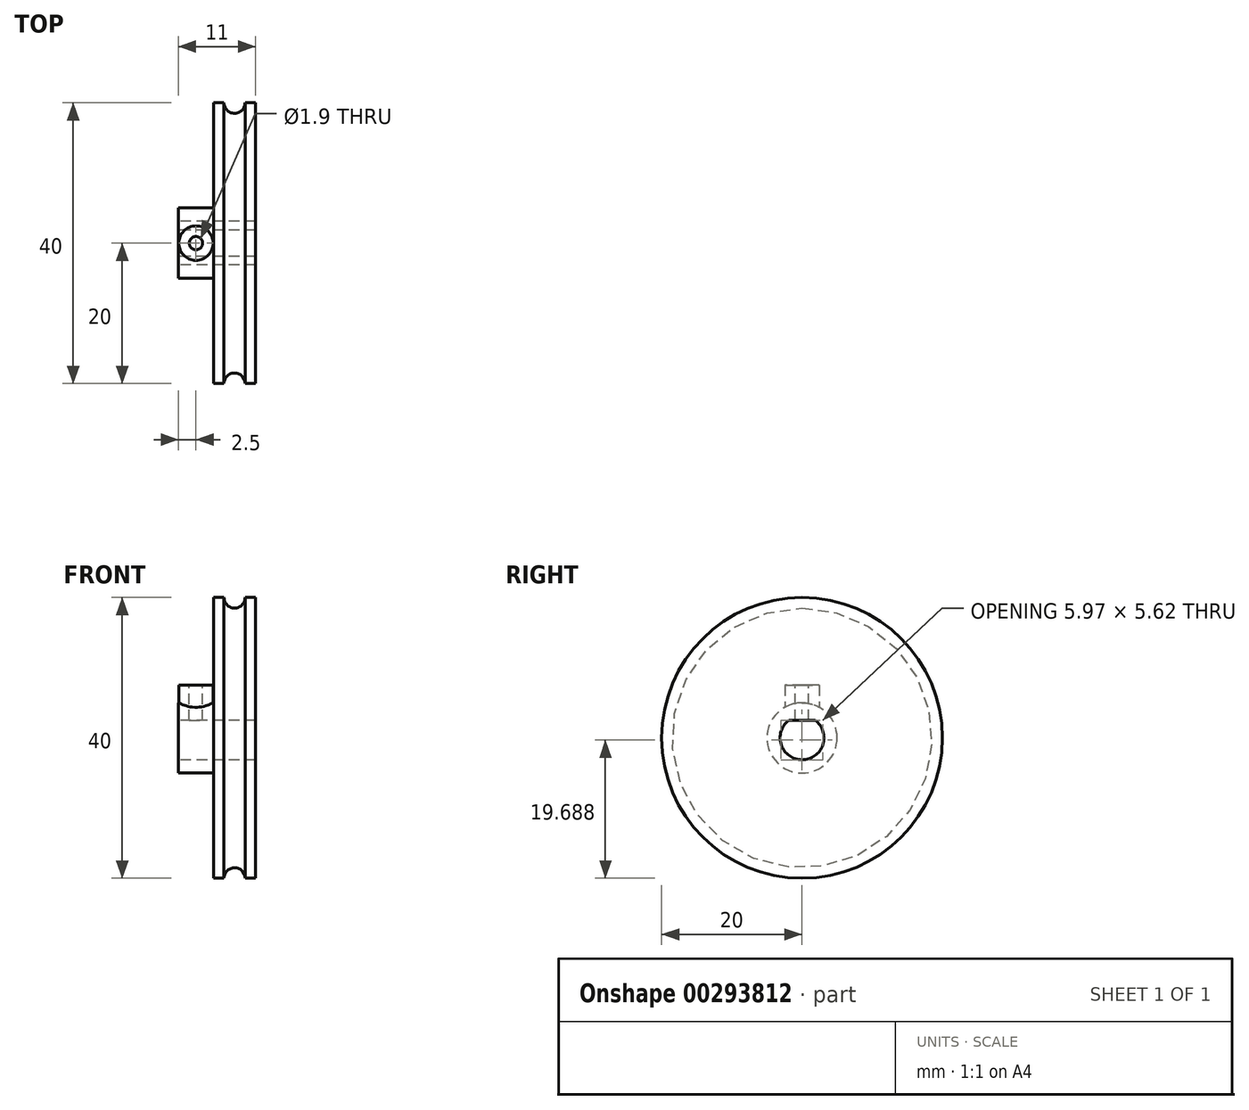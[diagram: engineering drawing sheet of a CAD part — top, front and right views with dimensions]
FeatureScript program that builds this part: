
annotation { "Feature Type Name" : "Feature", "Feature Type Description" : "" }
export const myFeature = defineFeature(function(context is Context, id is Id, definition is map)
    precondition{}
    {
        {
            var Q0;
            Q0=qCreatedBy(makeId("Top.planeOp"),FACE);
            var sketch = newSketch(context, id + "F0", { "sketchPlane" : qUnion([Q0])});
            skLineSegment(sketch, "E0", {"start": v(1.5, 0) * mm, "end": v(1.5, 20) * mm});
            skLineSegment(sketch, "E1", {"start": v(-4.5, 0) * mm, "end": v(-4.5, 20) * mm});
            skLineSegment(sketch, "E2", {"start": v(-4.5, 0) * mm, "end": v(1.5, 0) * mm});
            skLineSegment(sketch, "E3", {"start": v(-4.5, 20) * mm, "end": v(-3, 20) * mm});
            skLineSegment(sketch, "E4", {"start": v(1.5, 20) * mm, "end": v(0, 20) * mm});
            skArc(sketch, "E5", {"start": v(-3, 20) * mm, "mid": v(-1.5, 18.5) * mm, "end": v(0, 20) * mm});
            skSolve(sketch);
        }
        {
            var Q0;
            Q0 = qSketchRegion(id + "F0", true);
            var Q1;
            Q1=sQuery(id+"F0.wireOp",EDGE,"E2");
            revolve(context, id + "F1", {"entities" : qUnion([Q0]), "axis" : qUnion([Q1]), "revolveType" : RevolveType.FULL});
        }
        {
            var Q0;
            Q0=makeQuery(id+"F1.opRevolve","SWEPT_FACE",FACE,{"disambiguationData":[OSD([sQuery(id+"F0.wireOp",EDGE,"E1")])]});
            cPlane(context, id + "F2", {"entities" : qUnion([Q0]), "cplaneType" : CPlaneType.OFFSET, "offset" : 0 * mm, "width" : 150 * mm, "height" : 150 * mm});
        }
        {
            var Q0;
            Q0=qCreatedBy(id+"F2.planeOp",FACE);
            var sketch = newSketch(context, id + "F3", { "sketchPlane" : qUnion([Q0])});
            skCircle(sketch, "E6", {"center": v(0, 0) * mm, "radius": 5 * mm});
            skSolve(sketch);
        }
        {
            var Q0;
            Q0 = qSketchRegion(id + "F3", true);
            extrude(context, id + "F4", {"entities" : qUnion([Q0]), "operationType" : NewBodyOperationType.ADD, "depth" : 5 * mm});
        }
        {
            var Q0;
            Q0=makeQuery(id+"F4.opExtrude","CAP_FACE",FACE,{"disambiguationData":[OSD([sQuery(id+"F3.wireOp",EDGE,"E6")])],"isStart":false});
            cPlane(context, id + "F5", {"entities" : qUnion([Q0]), "cplaneType" : CPlaneType.OFFSET, "offset" : 0 * mm, "width" : 150 * mm, "height" : 150 * mm});
        }
        {
            var Q0;
            Q0=qCreatedBy(id+"F5.planeOp",FACE);
            var sketch = newSketch(context, id + "F6", { "sketchPlane" : qUnion([Q0])});
            skArc(sketch, "E7", {"start": v(-1.88, 2.5) * mm, "mid": v(0, -3.12) * mm, "end": v(1.87, 2.5) * mm});
            skLineSegment(sketch, "E8", {"start": v(-1.88, 2.5) * mm, "end": v(1.88, 2.5) * mm});
            skSolve(sketch);
        }
        {
            var Q0;
            Q0 = qSketchRegion(id + "F6", true);
            var Q1;
            Q1=makeQuery(id+"F1.opRevolve","SWEPT_FACE",FACE,{"disambiguationData":[OSD([sQuery(id+"F0.wireOp",EDGE,"E0")])]});
            extrude(context, id + "F7", {"entities" : qUnion([Q0]), "operationType" : NewBodyOperationType.REMOVE, "endBound" : BoundingType.UP_TO_SURFACE, "oppositeDirection" : true, "endBoundEntityFace" : qUnion([Q1]), "depth" : 25 * mm});
        }
        {
            var Q0;
            Q0=makeQuery(id+"F7.boolean.opBoolean","COPY",FACE,{"derivedFrom":makeQuery(id+"F7.opExtrude","SWEPT_FACE",FACE,{"disambiguationData":[OSD([sQuery(id+"F6.wireOp",EDGE,"E8")])]})});
            cPlane(context, id + "F8", {"entities" : qUnion([Q0]), "cplaneType" : CPlaneType.OFFSET, "offset" : 0 * mm, "width" : 150 * mm, "height" : 150 * mm});
        }
        {
            var Q0;
            Q0=qCreatedBy(id+"F8.planeOp",FACE);
            var sketch = newSketch(context, id + "F9", { "sketchPlane" : qUnion([Q0])});
            skLineSegment(sketch, "E9", {"start": v(-4.5, -5) * mm, "end": v(-9.5, -5) * mm, "construction": true});
            skLineSegment(sketch, "E10", {"start": v(-9.5, 5) * mm, "end": v(-4.5, 5) * mm, "construction": true});
            skCircle(sketch, "E11", {"center": v(-7, 0) * mm, "radius": 2.45 * mm});
            skPoint(sketch, "E11.centerSnap0", {"position": v(-7, -5) * mm});
            skSolve(sketch);
        }
        {
            var Q0;
            Q0 = qSketchRegion(id + "F9", true);
            var Q1;
            Q1=makeQuery(id+"F4.opExtrude","SWEPT_FACE",FACE,{"disambiguationData":[OSD([sQuery(id+"F3.wireOp",EDGE,"E6")])]});
            extrude(context, id + "F10", {"entities" : qUnion([Q0]), "operationType" : NewBodyOperationType.ADD, "oppositeDirection" : true, "endBoundEntityFace" : qUnion([Q1]), "depth" : 5 * mm});
        }
        {
            var Q0;
            Q0=makeQuery(id+"F10.opExtrude","CAP_FACE",FACE,{"disambiguationData":[OSD([sQuery(id+"F9.wireOp",EDGE,"E11")])],"isStart":false});
            cPlane(context, id + "F11", {"entities" : qUnion([Q0]), "cplaneType" : CPlaneType.OFFSET, "offset" : 0 * mm, "width" : 150 * mm, "height" : 150 * mm});
        }
        {
            var Q0;
            Q0=qCreatedBy(id+"F11.planeOp",FACE);
            var sketch = newSketch(context, id + "F12", { "sketchPlane" : qUnion([Q0])});
            skCircle(sketch, "E12.0.0", {"center": v(-7, 0) * mm, "radius": 2.45 * mm, "construction": true});
            skCircle(sketch, "E13", {"center": v(-7, 0) * mm, "radius": 0.95 * mm});
            skSolve(sketch);
        }
        {
            var Q0;
            Q0 = qSketchRegion(id + "F12", true);
            var Q1;
            Q1=makeQuery(id+"F7.boolean.opBoolean","COPY",FACE,{"derivedFrom":makeQuery(id+"F7.opExtrude","SWEPT_FACE",FACE,{"disambiguationData":[OSD([sQuery(id+"F6.wireOp",EDGE,"E8")])]})});
            extrude(context, id + "F13", {"entities" : qUnion([Q0]), "operationType" : NewBodyOperationType.REMOVE, "endBound" : BoundingType.UP_TO_SURFACE, "oppositeDirection" : true, "endBoundEntityFace" : qUnion([Q1]), "depth" : 25 * mm});
        }
    });
